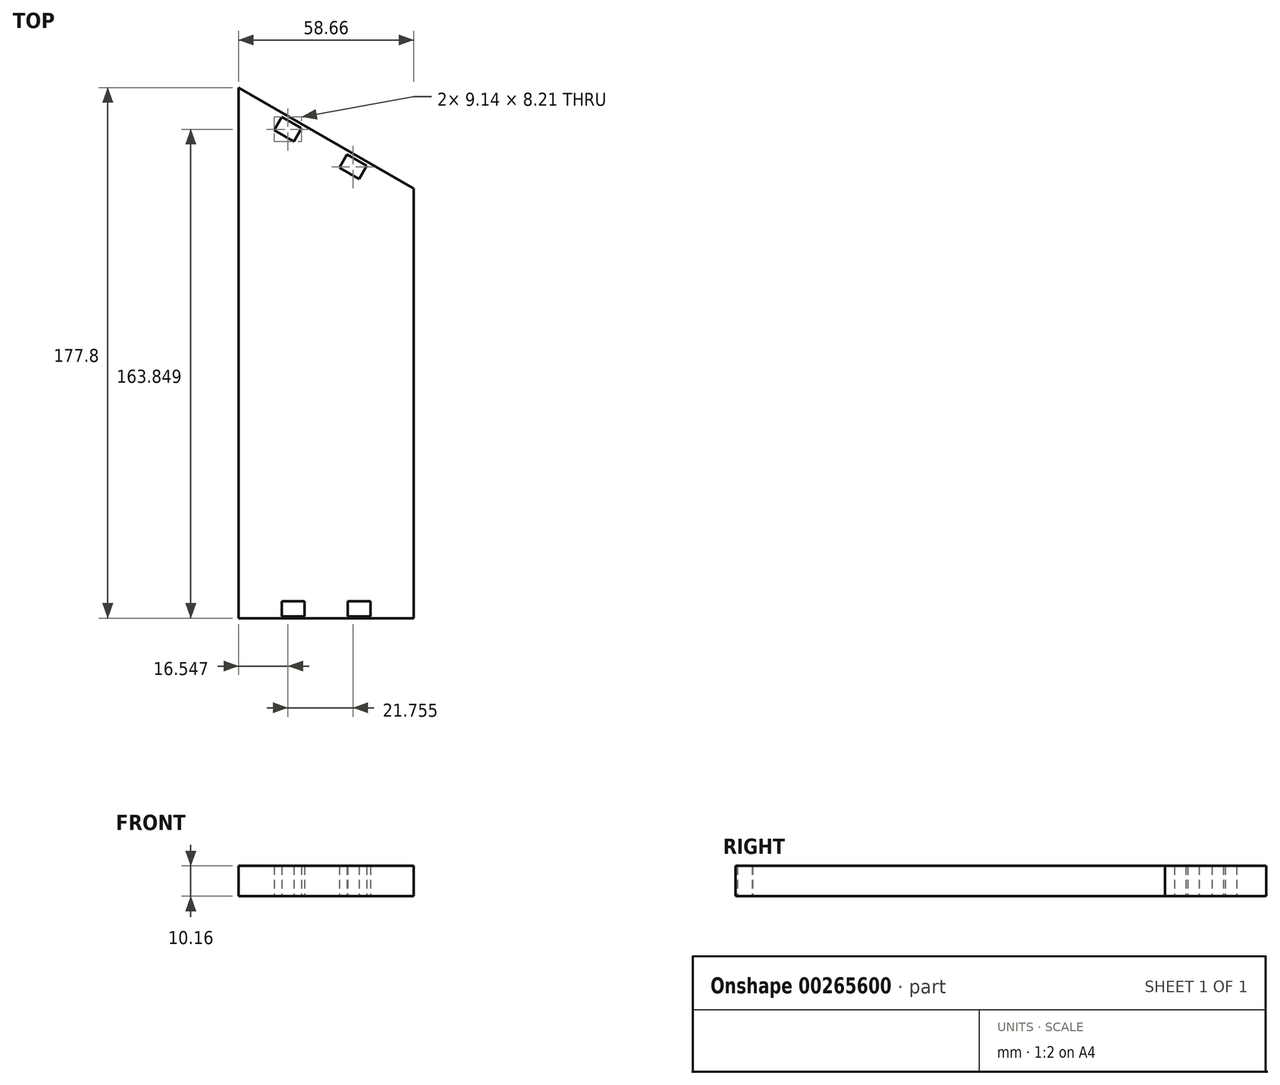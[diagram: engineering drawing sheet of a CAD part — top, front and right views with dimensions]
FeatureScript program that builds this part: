
annotation { "Feature Type Name" : "Feature", "Feature Type Description" : "" }
export const myFeature = defineFeature(function(context is Context, id is Id, definition is map)
    precondition{}
    {
        {
            var Q0;
            Q0=qCreatedBy(makeId("Top.planeOp"),FACE);
            var sketch = newSketch(context, id + "F0", { "sketchPlane" : qUnion([Q0])});
            skLineSegment(sketch, "E0", {"start": v(-23.12, 54.33) * mm, "end": v(-23.12, -123.47) * mm});
            skLineSegment(sketch, "E1", {"start": v(-23.12, -123.47) * mm, "end": v(35.54, -123.47) * mm});
            skLineSegment(sketch, "E2", {"start": v(35.54, -123.47) * mm, "end": v(35.54, 20.47) * mm});
            skLineSegment(sketch, "E3", {"start": v(35.54, 20.47) * mm, "end": v(-23.12, 54.33) * mm});
            skLineSegment(sketch, "E4", {"start": v(-23.12, -117.75) * mm, "end": v(35.54, -117.75) * mm, "construction": true});
            skLineSegment(sketch, "E5.bottom", {"start": v(-8.67, -117.75) * mm, "end": v(-1.05, -117.75) * mm});
            skLineSegment(sketch, "E5.top", {"start": v(-8.67, -122.83) * mm, "end": v(-1.05, -122.83) * mm});
            skLineSegment(sketch, "E5.left", {"start": v(-8.67, -117.75) * mm, "end": v(-8.67, -122.83) * mm});
            skLineSegment(sketch, "E5.right", {"start": v(-1.05, -117.75) * mm, "end": v(-1.05, -122.83) * mm});
            skLineSegment(sketch, "E6.top", {"start": v(8.8, -123.47) * mm, "end": v(25.31, -123.47) * mm});
            skLineSegment(sketch, "E7.bottom", {"start": v(13.4, -117.76) * mm, "end": v(21.02, -117.76) * mm});
            skLineSegment(sketch, "E7.top", {"start": v(13.4, -122.84) * mm, "end": v(21.02, -122.84) * mm});
            skLineSegment(sketch, "E7.left", {"start": v(13.4, -117.76) * mm, "end": v(13.4, -122.84) * mm});
            skLineSegment(sketch, "E7.right", {"start": v(21.02, -117.76) * mm, "end": v(21.02, -122.84) * mm});
            skLineSegment(sketch, "E8", {"start": v(-23.12, 47) * mm, "end": v(35.54, 13.13) * mm, "construction": true});
            skLineSegment(sketch, "E9", {"start": v(-8.6, 44.48) * mm, "end": v(-11.14, 40.08) * mm});
            skLineSegment(sketch, "E10", {"start": v(-11.14, 40.08) * mm, "end": v(-4.54, 36.27) * mm});
            skLineSegment(sketch, "E11", {"start": v(-41.2, 23.03) * mm, "end": v(-7.16, 81.98) * mm, "construction": true});
            skLineSegment(sketch, "E12", {"start": v(18.57, -8.92) * mm, "end": v(55.65, 55.31) * mm, "construction": true});
            skLineSegment(sketch, "E13.top", {"start": v(10.61, 27.52) * mm, "end": v(17.21, 23.71) * mm});
            skLineSegment(sketch, "E13.left", {"start": v(13.15, 31.92) * mm, "end": v(10.61, 27.52) * mm});
            skLineSegment(sketch, "E14", {"start": v(-4.54, 36.27) * mm, "end": v(-2, 40.67) * mm});
            skLineSegment(sketch, "E15", {"start": v(-8.6, 44.48) * mm, "end": v(-2, 40.67) * mm});
            skLineSegment(sketch, "E16", {"start": v(17.21, 23.71) * mm, "end": v(19.75, 28.11) * mm});
            skLineSegment(sketch, "E17", {"start": v(13.15, 31.92) * mm, "end": v(19.75, 28.11) * mm});
            skSolve(sketch);
        }
        {
            var Q0;
            {var subQ24=sQuery(id+"F0.wireOp",EDGE,"E0");Q0=makeQuery(id+"F0.imprint","IMPRINT",FACE,{"disambiguationData":[TD([[makeQuery(id+"F0.imprint","IMPRINT",EDGE,{"derivedFrom":subQ24}),1.0]])]});}
            extrude(context, id + "F1", {"entities" : qUnion([Q0]), "depth" : 10.16 * mm});
        }
    });
